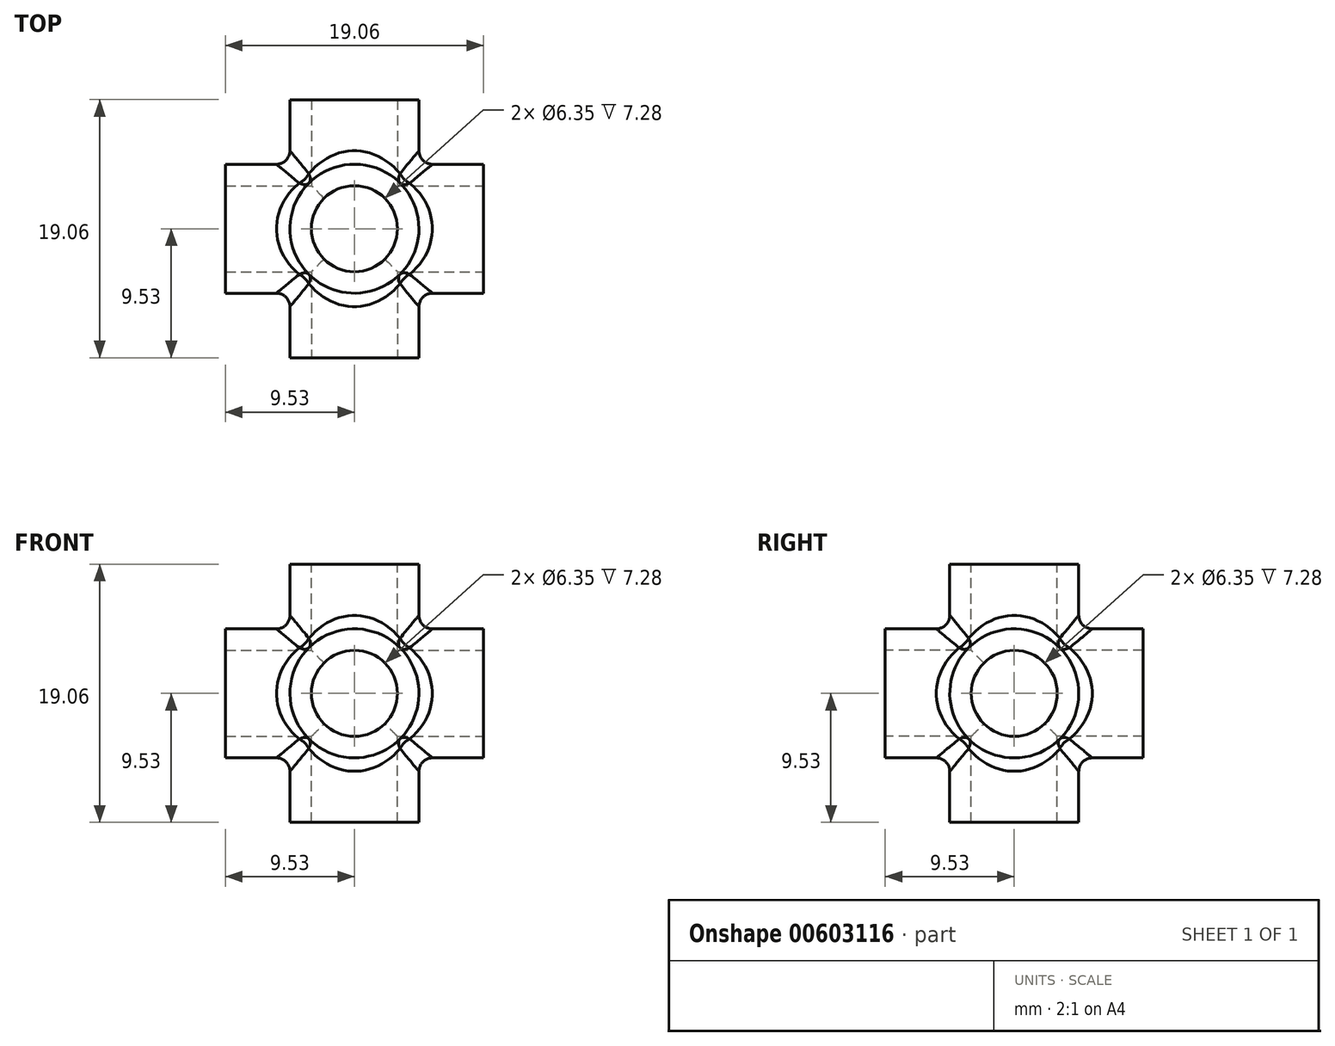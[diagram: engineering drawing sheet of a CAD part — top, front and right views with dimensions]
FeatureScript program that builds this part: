
annotation { "Feature Type Name" : "Feature", "Feature Type Description" : "" }
export const myFeature = defineFeature(function(context is Context, id is Id, definition is map)
    precondition{}
    {
        {
            var Q0;
            Q0=qCreatedBy(makeId("Front.planeOp"),FACE);
            var sketch = newSketch(context, id + "F0", { "sketchPlane" : qUnion([Q0])});
            skCircle(sketch, "E0", {"center": v(0, 0) * mm, "radius": 4.76 * mm});
            skSolve(sketch);
        }
        {
            var Q0;
            Q0=qSketchRegion(id+"F0",true);
            extrude(context, id + "F1", {"entities" : qUnion([Q0]), "endBound" : BoundingType.SYMMETRIC, "depth" : 19.05 * mm});
        }
        {
            var Q0;
            Q0=qCreatedBy(makeId("Right.planeOp"),FACE);
            var sketch = newSketch(context, id + "F2", { "sketchPlane" : qUnion([Q0])});
            skCircle(sketch, "E1", {"center": v(0, 0) * mm, "radius": 4.76 * mm});
            skSolve(sketch);
        }
        {
            var Q0;
            Q0=qSketchRegion(id+"F2",true);
            extrude(context, id + "F3", {"entities" : qUnion([Q0]), "operationType" : NewBodyOperationType.ADD, "endBound" : BoundingType.SYMMETRIC, "depth" : 19.05 * mm});
        }
        {
            var Q0;
            Q0=qCreatedBy(makeId("Top.planeOp"),FACE);
            var sketch = newSketch(context, id + "F4", { "sketchPlane" : qUnion([Q0])});
            skCircle(sketch, "E2", {"center": v(0, 0) * mm, "radius": 4.76 * mm});
            skSolve(sketch);
        }
        {
            var Q0;
            Q0=qSketchRegion(id+"F4",true);
            extrude(context, id + "F5", {"entities" : qUnion([Q0]), "operationType" : NewBodyOperationType.ADD, "endBound" : BoundingType.SYMMETRIC, "depth" : 19.05 * mm});
        }
        {
            var Q0;
            Q0=makeQuery(id+"F1.opExtrude","CAP_FACE",FACE,{"disambiguationData":[OSD([sQuery(id+"F0.wireOp",EDGE,"E0")])],"isStart":false});
            var sketch = newSketch(context, id + "F6", { "sketchPlane" : qUnion([Q0])});
            skCircle(sketch, "E3", {"center": v(0, 0) * mm, "radius": 3.18 * mm});
            skSolve(sketch);
        }
        {
            var Q0;
            Q0=qSketchRegion(id+"F6",true);
            extrude(context, id + "F7", {"entities" : qUnion([Q0]), "operationType" : NewBodyOperationType.REMOVE, "oppositeDirection" : true, "depth" : 20 * mm});
        }
        {
            var Q0;
            Q0=makeQuery(id+"F3.opExtrude","CAP_FACE",FACE,{"disambiguationData":[OSD([sQuery(id+"F2.wireOp",EDGE,"E1")])],"isStart":false});
            var sketch = newSketch(context, id + "F8", { "sketchPlane" : qUnion([Q0])});
            skCircle(sketch, "E4", {"center": v(0, 0) * mm, "radius": 3.18 * mm});
            skSolve(sketch);
        }
        {
            var Q0;
            Q0=makeQuery(id+"F8.imprint","IMPRINT",FACE,{"disambiguationData":[TD([[makeQuery(id+"F8.imprint","IMPRINT",EDGE,{"derivedFrom":sQuery(id+"F8.wireOp",EDGE,"E4")}),1.0]])]});
            extrude(context, id + "F9", {"entities" : qUnion([Q0]), "operationType" : NewBodyOperationType.REMOVE, "oppositeDirection" : true, "depth" : 20 * mm});
        }
        {
            var Q0;
            Q0=makeQuery(id+"F5.opExtrude","CAP_FACE",FACE,{"disambiguationData":[OSD([sQuery(id+"F4.wireOp",EDGE,"E2")])],"isStart":false});
            var sketch = newSketch(context, id + "F10", { "sketchPlane" : qUnion([Q0])});
            skCircle(sketch, "E5", {"center": v(0, 0) * mm, "radius": 3.18 * mm});
            skSolve(sketch);
        }
        {
            var Q0;
            Q0=makeQuery(id+"F10.imprint","IMPRINT",FACE,{"disambiguationData":[TD([[makeQuery(id+"F10.imprint","IMPRINT",EDGE,{"derivedFrom":sQuery(id+"F10.wireOp",EDGE,"E5")}),1.0]])]});
            extrude(context, id + "F11", {"entities" : qUnion([Q0]), "operationType" : NewBodyOperationType.REMOVE, "oppositeDirection" : true, "depth" : 20 * mm});
        }
        {
            var Q0;
            {var subQ0=sQuery(id+"F2.wireOp",EDGE,"E1");var subQ1=makeQuery(id+"F3.opExtrude","SWEPT_FACE",FACE,{"disambiguationData":[OSD([subQ0])]});Q0=makeQuery(id+"F5.boolean.opBoolean","INTERSECT",EDGE,{"disambiguationData":[OD(1.0)],"derivedFrom":[makeQuery(id+"F3.boolean.opBoolean","SPLIT",FACE,{"disambiguationData":[TD([makeQuery(id+"F3.opExtrude","CAP_FACE",FACE,{"disambiguationData":[OSD([subQ0])],"isStart":true})])],"derivedFrom":subQ1}),makeQuery(id+"F5.opExtrude","SWEPT_FACE",FACE,{"disambiguationData":[OSD([sQuery(id+"F4.wireOp",EDGE,"E2")])]})]});}
            var Q1;
            {var subQ0=sQuery(id+"F0.wireOp",EDGE,"E0");var subQ1=makeQuery(id+"F1.opExtrude","SWEPT_FACE",FACE,{"disambiguationData":[OSD([subQ0])]});Q1=makeQuery(id+"F5.boolean.opBoolean","INTERSECT",EDGE,{"disambiguationData":[OD(1.0)],"derivedFrom":[makeQuery(id+"F3.boolean.opBoolean","SPLIT",FACE,{"disambiguationData":[TD([makeQuery(id+"F1.opExtrude","CAP_FACE",FACE,{"disambiguationData":[OSD([subQ0])],"isStart":false})])],"derivedFrom":subQ1}),makeQuery(id+"F5.opExtrude","SWEPT_FACE",FACE,{"disambiguationData":[OSD([sQuery(id+"F4.wireOp",EDGE,"E2")])]})]});}
            var Q2;
            Q2=makeQuery(id+"F3.boolean.opBoolean","INTERSECT",EDGE,{"disambiguationData":[OD(2.0)],"derivedFrom":[makeQuery(id+"F1.opExtrude","SWEPT_FACE",FACE,{"disambiguationData":[OSD([sQuery(id+"F0.wireOp",EDGE,"E0")])]}),makeQuery(id+"F3.opExtrude","SWEPT_FACE",FACE,{"disambiguationData":[OSD([sQuery(id+"F2.wireOp",EDGE,"E1")])]})]});
            var Q3;
            {var subQ0=sQuery(id+"F2.wireOp",EDGE,"E1");var subQ1=makeQuery(id+"F3.opExtrude","SWEPT_FACE",FACE,{"disambiguationData":[OSD([subQ0])]});Q3=makeQuery(id+"F5.boolean.opBoolean","INTERSECT",EDGE,{"disambiguationData":[OD(0.0)],"derivedFrom":[makeQuery(id+"F3.boolean.opBoolean","SPLIT",FACE,{"disambiguationData":[TD([makeQuery(id+"F3.opExtrude","CAP_FACE",FACE,{"disambiguationData":[OSD([subQ0])],"isStart":true})])],"derivedFrom":subQ1}),makeQuery(id+"F5.opExtrude","SWEPT_FACE",FACE,{"disambiguationData":[OSD([sQuery(id+"F4.wireOp",EDGE,"E2")])]})]});}
            var Q4;
            {var subQ0=sQuery(id+"F0.wireOp",EDGE,"E0");var subQ1=makeQuery(id+"F1.opExtrude","SWEPT_FACE",FACE,{"disambiguationData":[OSD([subQ0])]});Q4=makeQuery(id+"F5.boolean.opBoolean","INTERSECT",EDGE,{"disambiguationData":[OD(0.0)],"derivedFrom":[makeQuery(id+"F3.boolean.opBoolean","SPLIT",FACE,{"disambiguationData":[TD([makeQuery(id+"F1.opExtrude","CAP_FACE",FACE,{"disambiguationData":[OSD([subQ0])],"isStart":false})])],"derivedFrom":subQ1}),makeQuery(id+"F5.opExtrude","SWEPT_FACE",FACE,{"disambiguationData":[OSD([sQuery(id+"F4.wireOp",EDGE,"E2")])]})]});}
            var Q5;
            Q5=makeQuery(id+"F3.boolean.opBoolean","INTERSECT",EDGE,{"disambiguationData":[OD(3.0)],"derivedFrom":[makeQuery(id+"F1.opExtrude","SWEPT_FACE",FACE,{"disambiguationData":[OSD([sQuery(id+"F0.wireOp",EDGE,"E0")])]}),makeQuery(id+"F3.opExtrude","SWEPT_FACE",FACE,{"disambiguationData":[OSD([sQuery(id+"F2.wireOp",EDGE,"E1")])]})]});
            var Q6;
            {var subQ0=sQuery(id+"F2.wireOp",EDGE,"E1");var subQ1=makeQuery(id+"F3.opExtrude","SWEPT_FACE",FACE,{"disambiguationData":[OSD([subQ0])]});Q6=makeQuery(id+"F5.boolean.opBoolean","INTERSECT",EDGE,{"disambiguationData":[OD(1.0)],"derivedFrom":[makeQuery(id+"F3.boolean.opBoolean","SPLIT",FACE,{"disambiguationData":[TD([makeQuery(id+"F3.opExtrude","CAP_FACE",FACE,{"disambiguationData":[OSD([subQ0])],"isStart":false})])],"derivedFrom":subQ1}),makeQuery(id+"F5.opExtrude","SWEPT_FACE",FACE,{"disambiguationData":[OSD([sQuery(id+"F4.wireOp",EDGE,"E2")])]})]});}
            var Q7;
            {var subQ0=sQuery(id+"F2.wireOp",EDGE,"E1");var subQ1=makeQuery(id+"F3.opExtrude","SWEPT_FACE",FACE,{"disambiguationData":[OSD([subQ0])]});Q7=makeQuery(id+"F5.boolean.opBoolean","INTERSECT",EDGE,{"disambiguationData":[OD(0.0)],"derivedFrom":[makeQuery(id+"F3.boolean.opBoolean","SPLIT",FACE,{"disambiguationData":[TD([makeQuery(id+"F3.opExtrude","CAP_FACE",FACE,{"disambiguationData":[OSD([subQ0])],"isStart":false})])],"derivedFrom":subQ1}),makeQuery(id+"F5.opExtrude","SWEPT_FACE",FACE,{"disambiguationData":[OSD([sQuery(id+"F4.wireOp",EDGE,"E2")])]})]});}
            var Q8;
            Q8=makeQuery(id+"F3.boolean.opBoolean","INTERSECT",EDGE,{"disambiguationData":[OD(1.0)],"derivedFrom":[makeQuery(id+"F1.opExtrude","SWEPT_FACE",FACE,{"disambiguationData":[OSD([sQuery(id+"F0.wireOp",EDGE,"E0")])]}),makeQuery(id+"F3.opExtrude","SWEPT_FACE",FACE,{"disambiguationData":[OSD([sQuery(id+"F2.wireOp",EDGE,"E1")])]})]});
            var Q9;
            {var subQ0=sQuery(id+"F0.wireOp",EDGE,"E0");var subQ1=makeQuery(id+"F1.opExtrude","SWEPT_FACE",FACE,{"disambiguationData":[OSD([subQ0])]});Q9=makeQuery(id+"F5.boolean.opBoolean","INTERSECT",EDGE,{"disambiguationData":[OD(1.0)],"derivedFrom":[makeQuery(id+"F3.boolean.opBoolean","SPLIT",FACE,{"disambiguationData":[TD([makeQuery(id+"F1.opExtrude","CAP_FACE",FACE,{"disambiguationData":[OSD([subQ0])],"isStart":true})])],"derivedFrom":subQ1}),makeQuery(id+"F5.opExtrude","SWEPT_FACE",FACE,{"disambiguationData":[OSD([sQuery(id+"F4.wireOp",EDGE,"E2")])]})]});}
            var Q10;
            Q10=makeQuery(id+"F3.boolean.opBoolean","INTERSECT",EDGE,{"disambiguationData":[OD(0.0)],"derivedFrom":[makeQuery(id+"F1.opExtrude","SWEPT_FACE",FACE,{"disambiguationData":[OSD([sQuery(id+"F0.wireOp",EDGE,"E0")])]}),makeQuery(id+"F3.opExtrude","SWEPT_FACE",FACE,{"disambiguationData":[OSD([sQuery(id+"F2.wireOp",EDGE,"E1")])]})]});
            var Q11;
            {var subQ0=sQuery(id+"F0.wireOp",EDGE,"E0");var subQ1=makeQuery(id+"F1.opExtrude","SWEPT_FACE",FACE,{"disambiguationData":[OSD([subQ0])]});Q11=makeQuery(id+"F5.boolean.opBoolean","INTERSECT",EDGE,{"disambiguationData":[OD(0.0)],"derivedFrom":[makeQuery(id+"F3.boolean.opBoolean","SPLIT",FACE,{"disambiguationData":[TD([makeQuery(id+"F1.opExtrude","CAP_FACE",FACE,{"disambiguationData":[OSD([subQ0])],"isStart":true})])],"derivedFrom":subQ1}),makeQuery(id+"F5.opExtrude","SWEPT_FACE",FACE,{"disambiguationData":[OSD([sQuery(id+"F4.wireOp",EDGE,"E2")])]})]});}
            fillet(context, id + "F12", {"entities" : qUnion([Q0, Q1, Q2, Q3, Q4, Q5, Q6, Q7, Q8, Q9, Q10, Q11]), "radius" : 1 * mm, "tangentPropagation" : true, "allowEdgeOverflow" : false});
        }
    });
